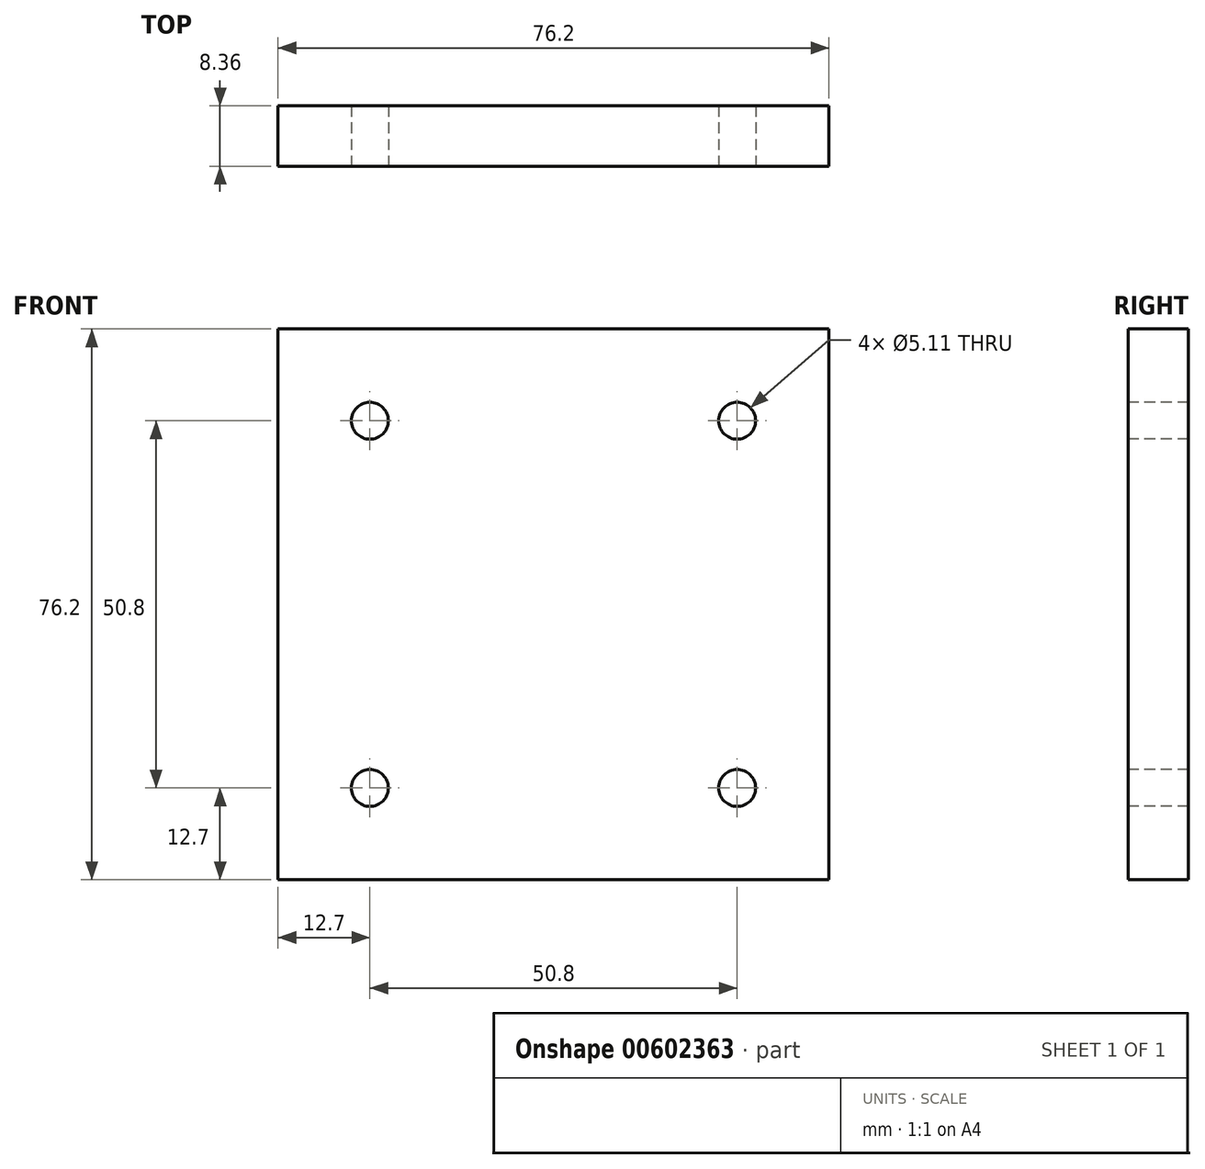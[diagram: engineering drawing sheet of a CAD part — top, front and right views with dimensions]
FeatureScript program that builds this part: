
annotation { "Feature Type Name" : "Feature", "Feature Type Description" : "" }
export const myFeature = defineFeature(function(context is Context, id is Id, definition is map)
    precondition{}
    {
        {
            var Q0;
            Q0=qCreatedBy(makeId("Front.planeOp"),FACE);
            var sketch = newSketch(context, id + "F0", { "sketchPlane" : qUnion([Q0])});
            skLineSegment(sketch, "E0.bottom", {"start": v(38.1, 38.1) * mm, "end": v(-38.1, 38.1) * mm});
            skLineSegment(sketch, "E0.top", {"start": v(38.1, -38.1) * mm, "end": v(-38.1, -38.1) * mm});
            skLineSegment(sketch, "E0.left", {"start": v(38.1, 38.1) * mm, "end": v(38.1, -38.1) * mm});
            skLineSegment(sketch, "E0.right", {"start": v(-38.1, 38.1) * mm, "end": v(-38.1, -38.1) * mm});
            skPoint(sketch, "E0.middle", {"position": v(0, 0) * mm});
            skSolve(sketch);
        }
        {
            var Q0;
            Q0 = qSketchRegion(id + "F0", true);
            extrude(context, id + "F1", {"entities" : qUnion([Q0]), "oppositeDirection" : true, "depth" : 8.36 * mm, "offsetDistance" : 25.4 * mm});
        }
        {
            var Q0;
            Q0=qCreatedBy(makeId("Front.planeOp"),FACE);
            var sketch = newSketch(context, id + "F2", { "sketchPlane" : qUnion([Q0])});
            skLineSegment(sketch, "E1", {"start": v(-38.1, 25.4) * mm, "end": v(-25.4, 25.4) * mm, "construction": true});
            skLineSegment(sketch, "E2", {"start": v(-25.4, 25.4) * mm, "end": v(-25.4, 38.1) * mm, "construction": true});
            skCircle(sketch, "E3", {"center": v(-25.4, 25.4) * mm, "radius": 2.55 * mm});
            skLineSegment(sketch, "E4", {"start": v(0, 0) * mm, "end": v(0, 38.1) * mm, "construction": true});
            skLineSegment(sketch, "E5", {"start": v(-38.1, 0) * mm, "end": v(38.1, 0) * mm, "construction": true});
            skLineSegment(sketch, "E6", {"start": v(0, 0) * mm, "end": v(0, -38.1) * mm, "construction": true});
            skCircle(sketch, "E7.MirrorC", {"center": v(25.4, 25.4) * mm, "radius": 2.55 * mm});
            skCircle(sketch, "E8.MirrorC", {"center": v(-25.4, -25.4) * mm, "radius": 2.55 * mm});
            skCircle(sketch, "E9.MirrorC", {"center": v(25.4, -25.4) * mm, "radius": 2.55 * mm});
            skSolve(sketch);
        }
        {
            var Q0;
            Q0 = qSketchRegion(id + "F2", true);
            extrude(context, id + "F3", {"entities" : qUnion([Q0]), "operationType" : NewBodyOperationType.REMOVE, "endBound" : BoundingType.THROUGH_ALL, "oppositeDirection" : true, "depth" : 25.4 * mm, "offsetDistance" : 25.4 * mm});
        }
    });
